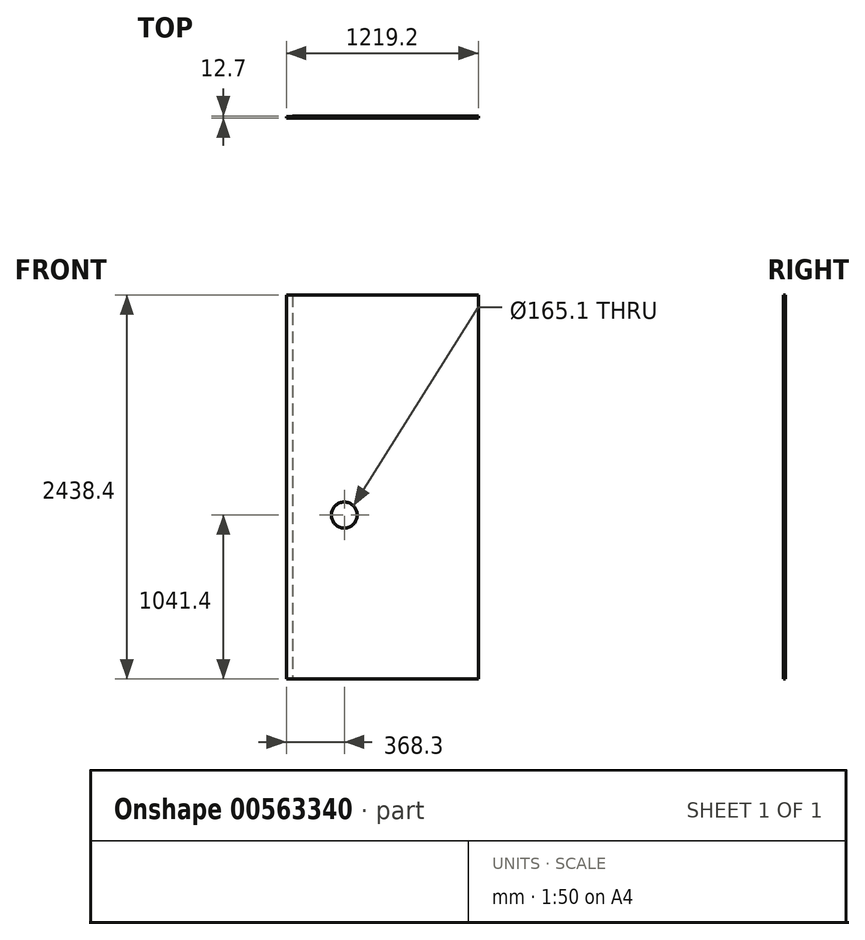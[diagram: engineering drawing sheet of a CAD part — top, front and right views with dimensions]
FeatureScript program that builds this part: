
annotation { "Feature Type Name" : "Feature", "Feature Type Description" : "" }
export const myFeature = defineFeature(function(context is Context, id is Id, definition is map)
    precondition{}
    {
        {
            var Q0;
            Q0=qCreatedBy(makeId("Top.planeOp"),FACE);
            var sketch = newSketch(context, id + "F0", { "sketchPlane" : qUnion([Q0])});
            skLineSegment(sketch, "E0.bottom", {"start": v(-609.6, -6.35) * mm, "end": v(609.6, -6.35) * mm});
            skLineSegment(sketch, "E0.top", {"start": v(-571.5, 6.35) * mm, "end": v(609.6, 6.35) * mm});
            skLineSegment(sketch, "E0.left", {"start": v(-609.6, -6.35) * mm, "end": v(-609.6, 3.18) * mm});
            skLineSegment(sketch, "E0.right", {"start": v(609.6, -6.35) * mm, "end": v(609.6, 6.35) * mm});
            skPoint(sketch, "E0.middle", {"position": v(0, 0) * mm});
            skLineSegment(sketch, "E1", {"start": v(-609.6, 3.18) * mm, "end": v(-571.5, 6.35) * mm});
            skPoint(sketch, "E2.orphan", {"position": v(-609.6, 6.35) * mm});
            skSolve(sketch);
        }
        {
            var Q0;
            Q0 = qSketchRegion(id + "F0", true);
            extrude(context, id + "F1", {"entities" : qUnion([Q0]), "depth" : 2438.4 * mm, "offsetDistance" : 25.4 * mm});
        }
        {
            var Q0;
            Q0=makeQuery(id+"F1.opExtrude","SWEPT_FACE",FACE,{"disambiguationData":[OSD([sQuery(id+"F0.wireOp",EDGE,"E0.bottom")])]});
            var sketch = newSketch(context, id + "F2", { "sketchPlane" : qUnion([Q0])});
            skLineSegment(sketch, "E3", {"start": v(-609.6, 1041.4) * mm, "end": v(609.6, 1041.4) * mm, "construction": true});
            skLineSegment(sketch, "E4", {"start": v(-241.3, 2438.4) * mm, "end": v(-241.3, 0) * mm, "construction": true});
            skCircle(sketch, "E5", {"center": v(-241.3, 1041.4) * mm, "radius": 82.55 * mm});
            skSolve(sketch);
        }
        {
            var Q0;
            Q0 = qSketchRegion(id + "F2", true);
            extrude(context, id + "F3", {"entities" : qUnion([Q0]), "operationType" : NewBodyOperationType.REMOVE, "oppositeDirection" : true, "depth" : 25.4 * mm, "offsetDistance" : 25.4 * mm});
        }
    });
